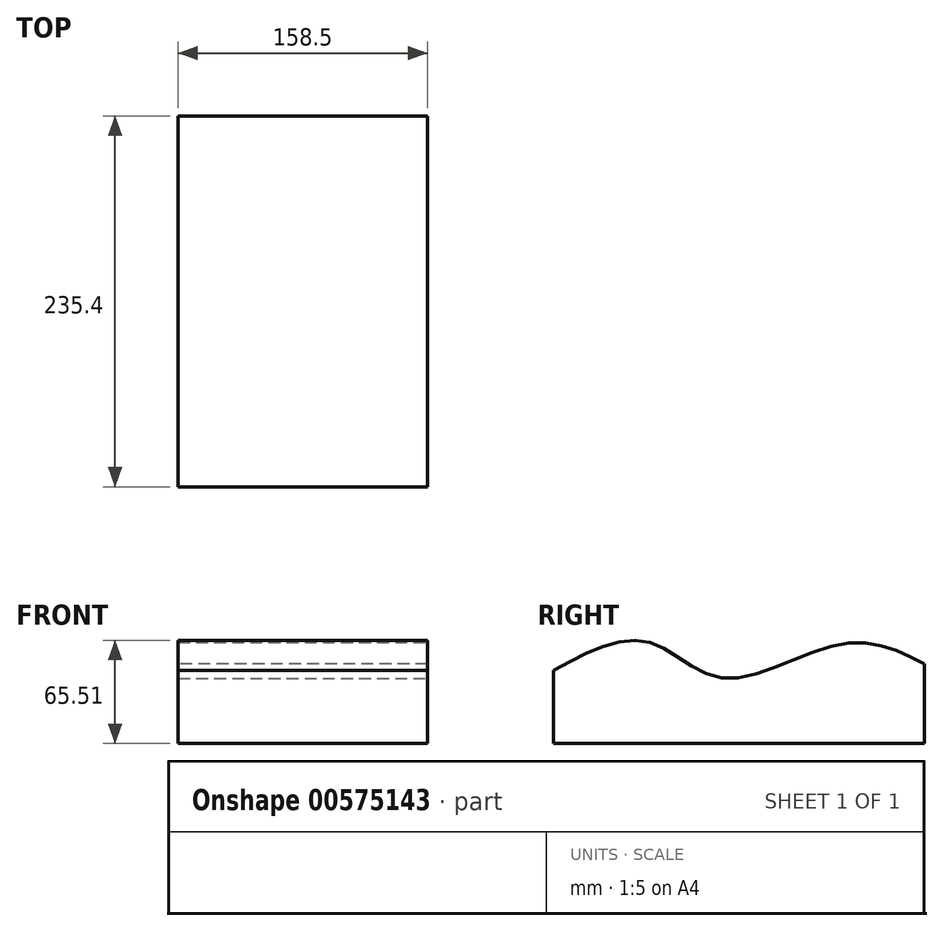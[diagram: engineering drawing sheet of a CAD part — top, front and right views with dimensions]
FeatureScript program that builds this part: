
annotation { "Feature Type Name" : "Feature", "Feature Type Description" : "" }
export const myFeature = defineFeature(function(context is Context, id is Id, definition is map)
    precondition{}
    {
        {
            var Q0;
            Q0=qCreatedBy(makeId("Right.planeOp"),FACE);
            var sketch = newSketch(context, id + "F0", { "sketchPlane" : qUnion([Q0])});
            skFitSpline(sketch, "E0", {"points": [v(-87.83, 46.37) * mm, v(-28.98, 64.64) * mm, v(20.5, 41.46) * mm, v(95.85, 63.3) * mm, v(147.57, 50.47) * mm], "startDerivative": vector(245.45, 133.58) * mm, "endDerivative": vector(196.91, -104.27) * mm});
            skLineSegment(sketch, "E1", {"start": v(-87.83, 46.37) * mm, "end": v(-87.83, 0) * mm});
            skLineSegment(sketch, "E2", {"start": v(-87.83, 0) * mm, "end": v(147.57, 0) * mm});
            skLineSegment(sketch, "E3", {"start": v(147.57, 0) * mm, "end": v(147.57, 50.47) * mm});
            skSolve(sketch);
        }
        {
            var Q0;
            Q0=makeQuery(id+"F0.imprint","IMPRINT",FACE,{"disambiguationData":[TD([[makeQuery(id+"F0.imprint","IMPRINT",EDGE,{"derivedFrom":sQuery(id+"F0.wireOp",EDGE,"E0")}),-1.0]])]});
            extrude(context, id + "F1", {"entities" : qUnion([Q0]), "depth" : 79.25 * mm, "offsetDistance" : 30.48 * mm, "hasSecondDirection" : true, "secondDirectionOppositeDirection" : true, "secondDirectionDepth" : 79.25 * mm});
        }
    });
